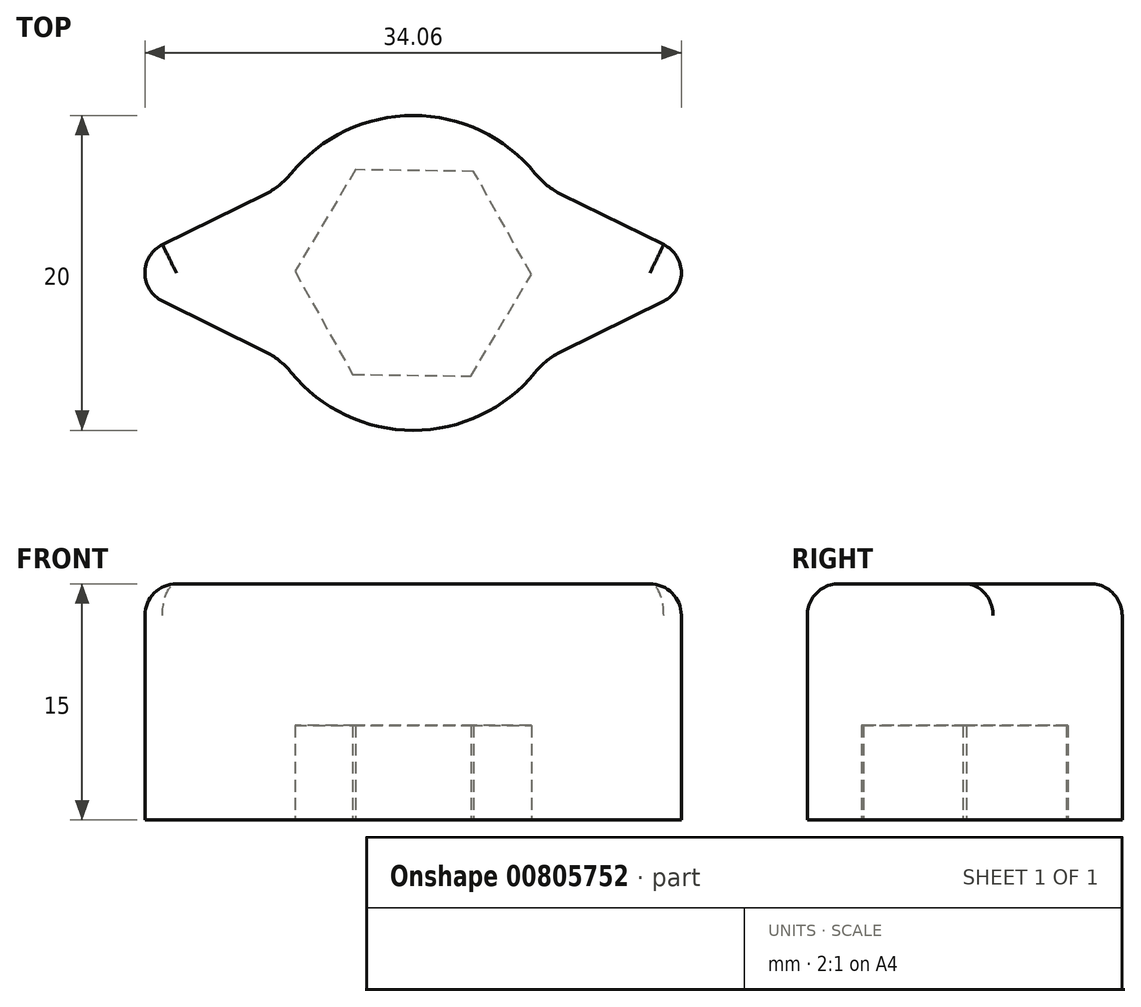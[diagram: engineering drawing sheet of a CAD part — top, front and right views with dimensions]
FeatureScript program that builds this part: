
annotation { "Feature Type Name" : "Feature", "Feature Type Description" : "" }
export const myFeature = defineFeature(function(context is Context, id is Id, definition is map)
    precondition{}
    {
        {
            var Q0;
            Q0=qCreatedBy(makeId("Top.planeOp"),FACE);
            var sketch = newSketch(context, id + "F0", { "sketchPlane" : qUnion([Q0])});
            skArc(sketch, "E0", {"start": v(-8.34, -5.52) * mm, "mid": v(0, -10) * mm, "end": v(8.34, -5.52) * mm});
            skLineSegment(sketch, "E1", {"start": v(0, 0) * mm, "end": v(0, -44.2) * mm, "construction": true});
            skLineSegment(sketch, "E2", {"start": v(0, 0) * mm, "end": v(61.46, 0) * mm, "construction": true});
            skLineSegment(sketch, "E3", {"start": v(8.34, 5.52) * mm, "end": v(18, 0.77) * mm});
            skLineSegment(sketch, "E4.MirrorCS", {"start": v(8.34, -5.52) * mm, "end": v(18, -0.77) * mm});
            skLineSegment(sketch, "E5", {"start": v(18, 0.77) * mm, "end": v(18, -0.77) * mm});
            skLineSegment(sketch, "E6.MirrorCS", {"start": v(-8.34, 5.52) * mm, "end": v(-18, 0.77) * mm});
            skLineSegment(sketch, "E7.MirrorCS", {"start": v(-8.34, -5.52) * mm, "end": v(-18, -0.77) * mm});
            skLineSegment(sketch, "E8.MirrorCS", {"start": v(-18, 0.77) * mm, "end": v(-18, -0.77) * mm});
            skArc(sketch, "E9.trimOffspring", {"start": v(8.34, 5.52) * mm, "mid": v(0, 10) * mm, "end": v(-8.34, 5.52) * mm});
            skSolve(sketch);
        }
        {
            var Q0;
            Q0=makeQuery(id+"F0.imprint","IMPRINT",FACE,{"disambiguationData":[TD([[makeQuery(id+"F0.imprint","IMPRINT",EDGE,{"derivedFrom":sQuery(id+"F0.wireOp",EDGE,"E0")}),1.0]])]});
            extrude(context, id + "F1", {"entities" : qUnion([Q0]), "depth" : 15 * mm, "offsetDistance" : 25 * mm});
        }
        {
            var Q0;
            Q0=makeQuery(id+"F1.opExtrude","CAP_FACE",FACE,{"disambiguationData":[OSD([sQuery(id+"F0.wireOp",EDGE,"E0"),sQuery(id+"F0.wireOp",EDGE,"E3"),sQuery(id+"F0.wireOp",EDGE,"E4.MirrorCS"),sQuery(id+"F0.wireOp",EDGE,"E5"),sQuery(id+"F0.wireOp",EDGE,"E6.MirrorCS"),sQuery(id+"F0.wireOp",EDGE,"E7.MirrorCS"),sQuery(id+"F0.wireOp",EDGE,"E8.MirrorCS"),sQuery(id+"F0.wireOp",EDGE,"E9.trimOffspring")])],"isStart":true});
            var sketch = newSketch(context, id + "F2", { "sketchPlane" : qUnion([Q0])});
            skCircle(sketch, "E10.cCircle", {"center": v(0, 0) * mm, "radius": 6.5 * mm, "construction": true});
            skLineSegment(sketch, "E10.0", {"start": v(-7.5, -0.1) * mm, "end": v(-3.84, 6.45) * mm});
            skLineSegment(sketch, "E10.1", {"start": v(-3.84, 6.45) * mm, "end": v(3.66, 6.55) * mm});
            skLineSegment(sketch, "E10.2", {"start": v(3.66, 6.55) * mm, "end": v(7.5, 0.1) * mm});
            skLineSegment(sketch, "E10.3", {"start": v(7.5, 0.1) * mm, "end": v(3.84, -6.45) * mm});
            skLineSegment(sketch, "E10.4", {"start": v(3.84, -6.45) * mm, "end": v(-3.66, -6.55) * mm});
            skLineSegment(sketch, "E10.5", {"start": v(-3.66, -6.55) * mm, "end": v(-7.5, -0.1) * mm});
            skPoint(sketch, "E10.0.midPoint", {"position": v(-5.67, 3.17) * mm});
            skSolve(sketch);
        }
        {
            var Q0;
            Q0=makeQuery(id+"F2.imprint","IMPRINT",FACE,{"disambiguationData":[TD([[makeQuery(id+"F2.imprint","IMPRINT",EDGE,{"derivedFrom":sQuery(id+"F2.wireOp",EDGE,"E10.0")}),-1.0]])]});
            extrude(context, id + "F3", {"entities" : qUnion([Q0]), "operationType" : NewBodyOperationType.REMOVE, "oppositeDirection" : true, "depth" : 6 * mm, "offsetDistance" : 25 * mm});
        }
        {
            var Q0;
            Q0=makeQuery(id+"F1.opExtrude","SWEPT_EDGE",EDGE,{"disambiguationData":[OSD([sQuery(id+"F0.wireOp",EDGE,"E7.MirrorCS"),sQuery(id+"F0.wireOp",EDGE,"E8.MirrorCS")])]});
            var Q1;
            Q1=makeQuery(id+"F1.opExtrude","SWEPT_EDGE",EDGE,{"disambiguationData":[OSD([sQuery(id+"F0.wireOp",EDGE,"E6.MirrorCS"),sQuery(id+"F0.wireOp",EDGE,"E8.MirrorCS")])]});
            var Q2;
            Q2=makeQuery(id+"F1.opExtrude","SWEPT_EDGE",EDGE,{"disambiguationData":[OSD([sQuery(id+"F0.wireOp",EDGE,"E4.MirrorCS"),sQuery(id+"F0.wireOp",EDGE,"E5")])]});
            var Q3;
            Q3=makeQuery(id+"F1.opExtrude","SWEPT_EDGE",EDGE,{"disambiguationData":[OSD([sQuery(id+"F0.wireOp",EDGE,"E3"),sQuery(id+"F0.wireOp",EDGE,"E5")])]});
            fillet(context, id + "F4", {"entities" : qUnion([Q0, Q1, Q2, Q3]), "radius" : 2 * mm, "tangentPropagation" : true, "allowEdgeOverflow" : false});
        }
        {
            var Q0;
            Q0=makeQuery(id+"F1.opExtrude","SWEPT_EDGE",EDGE,{"disambiguationData":[OSD([sQuery(id+"F0.wireOp",EDGE,"E6.MirrorCS"),sQuery(id+"F0.wireOp",EDGE,"E9.trimOffspring")])]});
            var Q1;
            Q1=makeQuery(id+"F1.opExtrude","SWEPT_EDGE",EDGE,{"disambiguationData":[OSD([sQuery(id+"F0.wireOp",EDGE,"E3"),sQuery(id+"F0.wireOp",EDGE,"E9.trimOffspring")])]});
            var Q2;
            Q2=makeQuery(id+"F1.opExtrude","SWEPT_EDGE",EDGE,{"disambiguationData":[OSD([sQuery(id+"F0.wireOp",EDGE,"E0"),sQuery(id+"F0.wireOp",EDGE,"E4.MirrorCS")])]});
            var Q3;
            Q3=makeQuery(id+"F1.opExtrude","SWEPT_EDGE",EDGE,{"disambiguationData":[OSD([sQuery(id+"F0.wireOp",EDGE,"E0"),sQuery(id+"F0.wireOp",EDGE,"E7.MirrorCS")])]});
            fillet(context, id + "F5", {"entities" : qUnion([Q0, Q1, Q2, Q3]), "radius" : 5 * mm, "tangentPropagation" : true, "allowEdgeOverflow" : false});
        }
        {
            var Q0;
            {var subQ0=sQuery(id+"F0.wireOp",EDGE,"E9.trimOffspring");var subQ1=sQuery(id+"F0.wireOp",EDGE,"E6.MirrorCS");Q0=makeQuery(id+"F5.opFillet","BLEND_EDGE",EDGE,{"blendedFrom":[makeQuery(id+"F1.opExtrude","SWEPT_EDGE",EDGE,{"disambiguationData":[OSD([subQ1,subQ0])]}),makeQuery(id+"F1.opExtrude","CAP_FACE",FACE,{"disambiguationData":[OSD([sQuery(id+"F0.wireOp",EDGE,"E0"),sQuery(id+"F0.wireOp",EDGE,"E3"),sQuery(id+"F0.wireOp",EDGE,"E4.MirrorCS"),sQuery(id+"F0.wireOp",EDGE,"E5"),subQ1,sQuery(id+"F0.wireOp",EDGE,"E7.MirrorCS"),sQuery(id+"F0.wireOp",EDGE,"E8.MirrorCS"),subQ0])],"isStart":false})],"blendedInto":[makeQuery(id+"F1.opExtrude","CAP_FACE",FACE,{"disambiguationData":[OSD([sQuery(id+"F0.wireOp",EDGE,"E0"),sQuery(id+"F0.wireOp",EDGE,"E3"),sQuery(id+"F0.wireOp",EDGE,"E4.MirrorCS"),sQuery(id+"F0.wireOp",EDGE,"E5"),subQ1,sQuery(id+"F0.wireOp",EDGE,"E7.MirrorCS"),sQuery(id+"F0.wireOp",EDGE,"E8.MirrorCS"),subQ0])],"isStart":false})]});}
            fillet(context, id + "F6", {"entities" : qUnion([Q0]), "radius" : 2 * mm, "tangentPropagation" : true, "allowEdgeOverflow" : false});
        }
        {
            var Q0;
            Q0=makeQuery(id+"F1.opExtrude","CAP_EDGE",EDGE,{"disambiguationData":[OSD([sQuery(id+"F0.wireOp",EDGE,"E7.MirrorCS")])],"isStart":false});
            fillet(context, id + "F7", {"entities" : qUnion([Q0]), "radius" : 2 * mm, "tangentPropagation" : true, "allowEdgeOverflow" : false});
        }
    });
